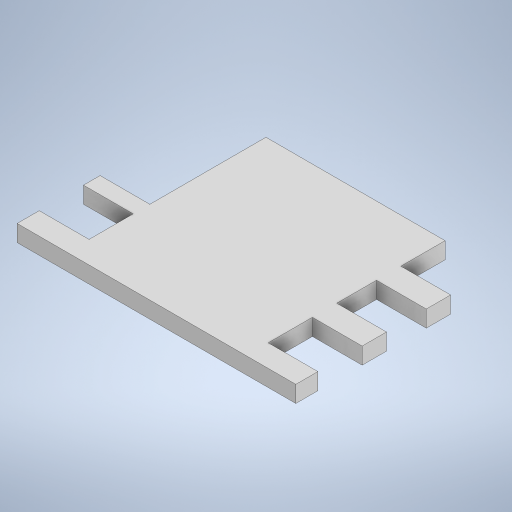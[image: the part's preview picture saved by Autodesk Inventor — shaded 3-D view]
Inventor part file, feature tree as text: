
AUTODESK INVENTOR PART (.ipt)
format: ipt  version: 2024 (Build 280153000, 153)  size: 269,824 bytes
history: native  units: mm
features: extrude x2, sketch x2
ambient origin geometry x8: Origin, YZ Plane, XZ Plane, XY Plane, X Axis, Y Axis, Z Axis, Center Point
bodies: Solid1 (feature_tree)
feature tree (4):
  extrude  "Extrusion1"  Depth=160.0mm
  extrude  "Extrusion3"  Depth=40.0mm
  sketch  "Sketch1"  dims[d0=162.0mm d1=160.0mm]
  sketch  "Sketch4"  dims[d2=40.0mm d5=40.0mm d7=45.0mm d8=45.0mm d9=20.0mm d10=45.0mm d11=15.0mm d12=45.0mm d13=207.0mm d14=15.0mm d15=15.0mm d16=0.0mm d25=36.0mm d26=22.0mm d27=0.0mm d28=0.0mm d29=22.0mm d30=15.0mm d31=0.0mm d32=0.0mm d33=45.0mm d34=45.0mm d35=45.0mm d36=36.0mm d37=22.0mm d38=22.0mm]
